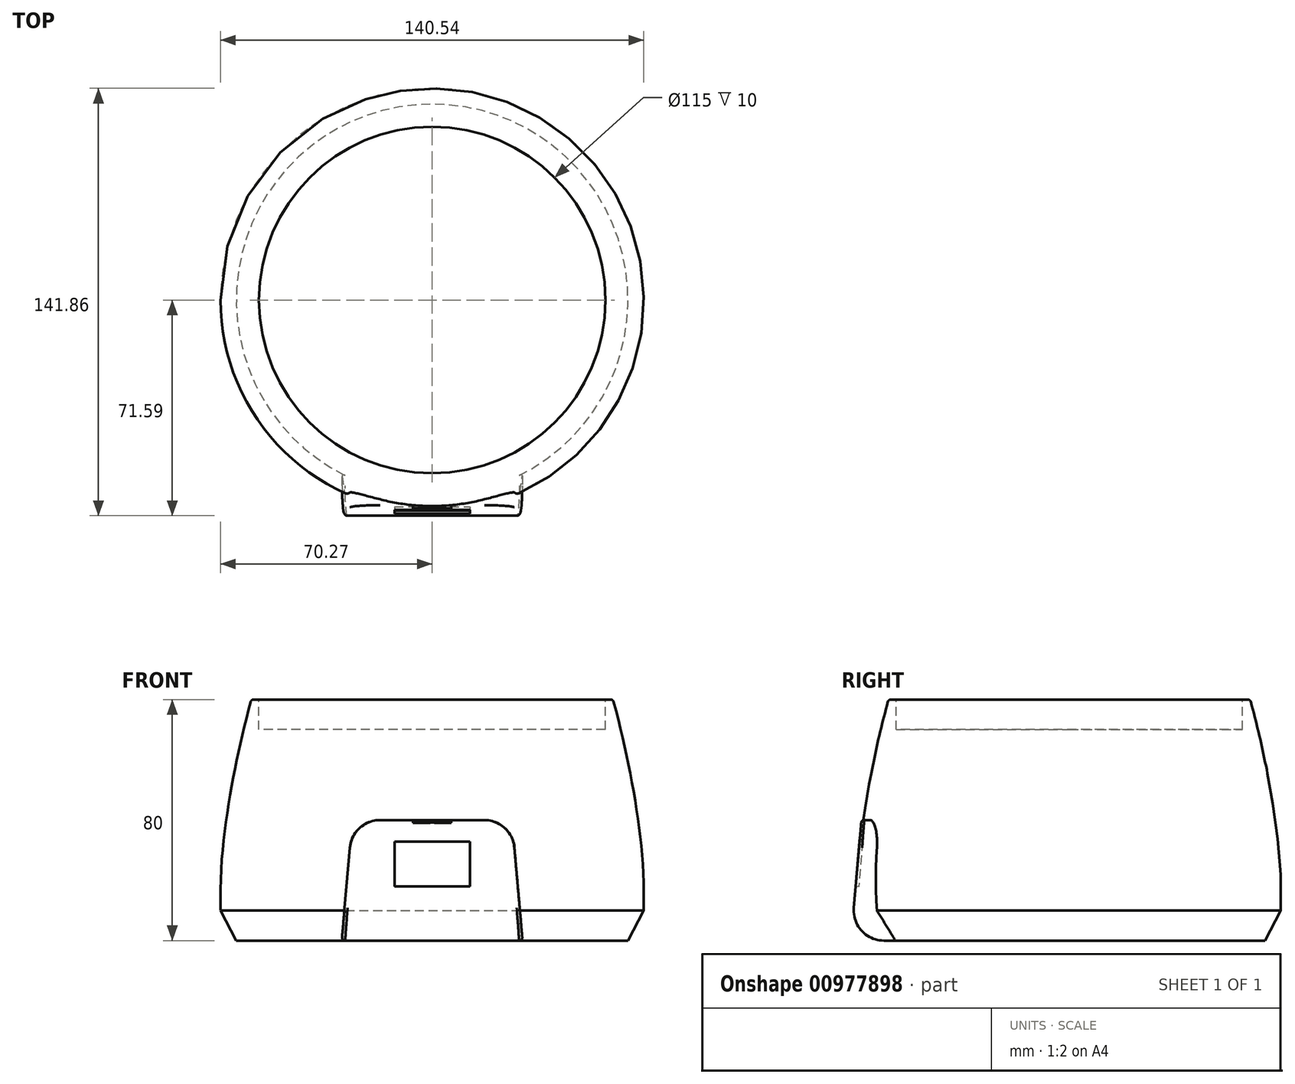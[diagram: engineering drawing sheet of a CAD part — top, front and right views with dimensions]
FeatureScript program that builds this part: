
annotation { "Feature Type Name" : "Feature", "Feature Type Description" : "" }
export const myFeature = defineFeature(function(context is Context, id is Id, definition is map)
    precondition{}
    {
        {
            var Q0;
            Q0=qCreatedBy(makeId("Front.planeOp"),FACE);
            var sketch = newSketch(context, id + "F0", { "sketchPlane" : qUnion([Q0])});
            skLineSegment(sketch, "E0", {"start": v(0, 0) * mm, "end": v(-65, 0) * mm});
            skLineSegment(sketch, "E1", {"start": v(0, 0) * mm, "end": v(0, 80) * mm});
            skLineSegment(sketch, "E2", {"start": v(0, 80) * mm, "end": v(-60, 80) * mm});
            skLineSegment(sketch, "E3", {"start": v(-70.2, 10) * mm, "end": v(-65, 0) * mm});
            skFitSpline(sketch, "E4", {"points": [v(-70.2, 10) * mm, v(-66.96, 48.92) * mm, v(-60, 80) * mm], "startDerivative": vector(-2.58, 81.22) * mm, "endDerivative": vector(18, 64.38) * mm});
            skLineSegment(sketch, "E5", {"start": v(-65, 0) * mm, "end": v(-65, 10) * mm});
            skLineSegment(sketch, "E6", {"start": v(-70.2, 10) * mm, "end": v(-69.9, 10) * mm});
            skLineSegment(sketch, "E7", {"start": v(-69.9, 10) * mm, "end": v(-69.9, 10.08) * mm});
            skLineSegment(sketch, "E8", {"start": v(-69.9, 10.08) * mm, "end": v(-70.2, 10.08) * mm});
            skSolve(sketch);
        }
        {
            var Q0;
            Q0 = qSketchRegion(id + "F0", true);
            var Q1;
            Q1=sQuery(id+"F0.wireOp",EDGE,"E1");
            revolve(context, id + "F1", {"surfaceOperationType" : NewSurfaceOperationType.NEW, "entities" : qUnion([Q0]), "axis" : qUnion([Q1]), "revolveType" : RevolveType.FULL});
        }
        {
            var Q0;
            Q0=qCreatedBy(makeId("Top.planeOp"),FACE);
            var sketch = newSketch(context, id + "F2", { "sketchPlane" : qUnion([Q0])});
            skLineSegment(sketch, "E9", {"start": v(0, 0) * mm, "end": v(0, -65) * mm});
            skLineSegment(sketch, "E10", {"start": v(0, -65) * mm, "end": v(-30, -65) * mm});
            skLineSegment(sketch, "E11", {"start": v(0, -65) * mm, "end": v(30, -65) * mm});
            skLineSegment(sketch, "E12", {"start": v(30, -65) * mm, "end": v(30, -72.5) * mm});
            skLineSegment(sketch, "E13", {"start": v(30, -72.5) * mm, "end": v(-30, -72.5) * mm});
            skLineSegment(sketch, "E14", {"start": v(-30, -72.5) * mm, "end": v(-30, -65) * mm});
            skLineSegment(sketch, "E15", {"start": v(-30, -65) * mm, "end": v(-30, -50) * mm});
            skLineSegment(sketch, "E16", {"start": v(-30, -50) * mm, "end": v(30, -50) * mm});
            skLineSegment(sketch, "E17", {"start": v(30, -50) * mm, "end": v(30, -65) * mm});
            skSolve(sketch);
        }
        {
            var Q0;
            Q0 = qSketchRegion(id + "F2", true);
            extrude(context, id + "F3", {"entities" : qUnion([Q0]), "operationType" : NewBodyOperationType.ADD, "depth" : 40 * mm, "offsetDistance" : 25 * mm, "hasDraft" : true, "draftAngle" : 5 * degree, "draftPullDirection" : true});
        }
        {
            var Q0;
            Q0=makeQuery(id+"F3.opExtrude","CAP_EDGE",EDGE,{"disambiguationData":[OSD([sQuery(id+"F2.wireOp",EDGE,"E14"),sQuery(id+"F2.wireOp",EDGE,"E15")])],"isStart":false});
            var Q1;
            Q1=makeQuery(id+"F3.opExtrude","CAP_EDGE",EDGE,{"disambiguationData":[OSD([sQuery(id+"F2.wireOp",EDGE,"E12"),sQuery(id+"F2.wireOp",EDGE,"E17")])],"isStart":false});
            fillet(context, id + "F4", {"entities" : qUnion([Q0, Q1]), "radius" : 10 * mm, "tangentPropagation" : true, "allowEdgeOverflow" : false});
        }
        {
            var Q0;
            Q0=makeQuery(id+"F3.opExtrude","CAP_EDGE",EDGE,{"disambiguationData":[OSD([sQuery(id+"F2.wireOp",EDGE,"E13")])],"isStart":true});
            fillet(context, id + "F5", {"entities" : qUnion([Q0]), "radius" : 10 * mm, "tangentPropagation" : true, "allowEdgeOverflow" : false});
        }
        {
            var Q0;
            Q0=makeQuery(id+"F1.opRevolve","SWEPT_FACE",FACE,{"disambiguationData":[OSD([sQuery(id+"F0.wireOp",EDGE,"E2")])]});
            var sketch = newSketch(context, id + "F6", { "sketchPlane" : qUnion([Q0])});
            skCircle(sketch, "E18", {"center": v(0, 0) * mm, "radius": 57.5 * mm});
            skSolve(sketch);
        }
        {
            var Q0;
            Q0 = qSketchRegion(id + "F6", true);
            extrude(context, id + "F7", {"entities" : qUnion([Q0]), "operationType" : NewBodyOperationType.REMOVE, "oppositeDirection" : true, "depth" : 10 * mm, "offsetDistance" : 25 * mm});
        }
        {
            var Q0;
            Q0=makeQuery(id+"F1.opRevolve","SWEPT_EDGE",EDGE,{"disambiguationData":[OSD([sQuery(id+"F0.wireOp",EDGE,"E2"),sQuery(id+"F0.wireOp",EDGE,"E4")])]});
            fillet(context, id + "F8", {"entities" : qUnion([Q0]), "radius" : 1 * mm, "tangentPropagation" : true, "allowEdgeOverflow" : false});
        }
        {
            var Q0;
            Q0=makeQuery(id+"F3.opExtrude","SWEPT_FACE",FACE,{"disambiguationData":[OSD([sQuery(id+"F2.wireOp",EDGE,"E13")])]});
            var sketch = newSketch(context, id + "F9", { "sketchPlane" : qUnion([Q0])});
            skLineSegment(sketch, "E19", {"start": v(0, 33.83) * mm, "end": v(0, 4.6) * mm});
            skLineSegment(sketch, "E20.bottom", {"start": v(-12.5, 26.71) * mm, "end": v(12.5, 26.71) * mm});
            skLineSegment(sketch, "E20.top", {"start": v(-12.5, 11.71) * mm, "end": v(12.5, 11.71) * mm});
            skLineSegment(sketch, "E20.left", {"start": v(-12.5, 26.71) * mm, "end": v(-12.5, 11.71) * mm});
            skLineSegment(sketch, "E20.right", {"start": v(12.5, 26.71) * mm, "end": v(12.5, 11.71) * mm});
            skPoint(sketch, "E20.middle", {"position": v(0, 19.21) * mm});
            skSolve(sketch);
        }
        {
            var Q0;
            Q0 = qSketchRegion(id + "F9", true);
            extrude(context, id + "F10", {"entities" : qUnion([Q0]), "operationType" : NewBodyOperationType.REMOVE, "oppositeDirection" : true, "depth" : 1 * mm, "offsetDistance" : 25 * mm});
        }
        {
            var Q0;
            Q0=makeQuery(id+"F5.opFillet","BLEND_FACE",FACE,{"disambiguationData":[OSD([sQuery(id+"F2.wireOp",EDGE,"E13")])]});
            fillet(context, id + "F11", {"entities" : qUnion([Q0]), "radius" : 1 * mm, "tangentPropagation" : true, "allowEdgeOverflow" : false});
        }
    });
